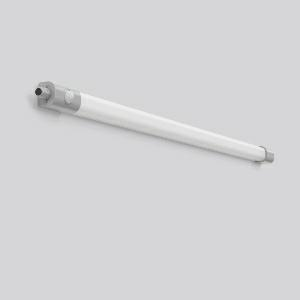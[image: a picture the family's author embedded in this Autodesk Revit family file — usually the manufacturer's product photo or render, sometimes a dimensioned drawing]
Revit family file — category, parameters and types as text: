
# Revit family: planox_eco_451219_009_19_9c9b
name_source: partatom
category: Lighting Fixtures
units: mm (PartAtom-declared; Revit-internal decimal feet)

## family parameters
Cut with Voids When Loaded = No
Host = Face
Light Source = No
Part Type = Normal
Room Calculation Point = No
Round Connector Dimension = Use Diameter
Shared = No

## types (1)
- MultiLumen 1 (1 x LED Modul 840, 4700 lm, 4000)
    Apparent Load = 33 VA
    CIE Flux Codes = 36 65 86 78 100
    Color Rendering = 80
    Color Temperature = 4000
    Default Elevation = 1800 mm
    Description = Series: Planox ECO
Moisture-proof luminaire with slim, flat housing. Side panels: plastic, grey polycarbonate, shockproof. Diffuser made of plastic (polycarbonate), opal, shockproof. Diffuser is extruded, prismatic inside and UV-resistant. Symmetrical light distribution. Homogeneous light distribution. Indirect light to illuminate the ceiling. Flexible installation thanks to sliding mounting brackets. Ideal for luminaire replacement. Ceiling mounting stainless steel brackets and triangular brackets for pendant mounting included in delivery. With integrated movement sensor. Converter encapsulated, integrated and permanently connected to the diffuser and side panel. Luminaire with integrated 4-phase through-wiring to connect multiple luminaires. Cable screw fittings for convenient wiring. Turn lock fastener on both sides for easy installation. MultiLumen: 2 steps adjustable luminous flux. Factory setting is H (high lumen). Luminaire with limited surface temperature in accordance with EN 60598-2-24 for use in environments in which a deposit of conductive dust on the luminaire can be expected. Qualified for use in the food and drink industry. 
Colour: grey
Length: 1700 mm
Width: 66 mm
Height: 71 mm
Lamp: LED
Socket: without socket
Colour temperature: 4000K
Colour rendering index (CRI): 80
System power: 33 W
Rated luminous flux: 4700 lm
Beam angle Down: 177° / 111°
Luminous efficiency: 142 lm/W
System power 2: 54 W
Rated luminous flux 2: 6800 lm
Luminous efficiency 2: 126 lm/W
Control gear: Regulated power supply
Protection class: II
Type of protection: IP 66
    Height = 71 mm
    Lamp = 1 x LED Modul 840
    Lamp Light Flux = 4700 lm
    Lamp count = 1
    Length = 1700 mm
    Lifetime = 50000 h
    Luminous efficacy = 142 lm/W
    Manufacturer = RZB
    ModVariant = No
    Model = 451219.009.19
    Mounting Place = Ceiling
    Mounting Type = Surface mounted
    Number of Poles = 1
    OnlyDefault = Yes
    Power Factor = 1
    Product Name = PLANOX ECO
    Product group = Surface mounted luminaires for moist/humid enviroments
    ProductGroupID = 308
    Protection Class = Protection class II
    Protection Degree = IP 66
    RLX_Detail_Level = 1
    RLX_Emergency_Light_Flux = 0 lm
    RLX_Emergency_Type = 0
    RLX_Emergency_Type_DB = No
    RlxData = <blob elided: 41297 chars, md5=61530dcb>
    Socket = socket
    Standby Power = 0 W
    System Light Flux = 4700 lm
    System Power = 33 W
    Type Comments = MultiLumen 1
    Type Image = 451219.009.19.jpg
    URL = http://relux.com
    VarID = multilumen_1
    Voltage = 230 V
    Voltage Range = 220-240 V
    Weight = 0.00 kg
    Width = 66 mm

## geometry (parser evidence)
native form markers: Blend x4, Sweep x14
no freeform markers — native parametric forms only
